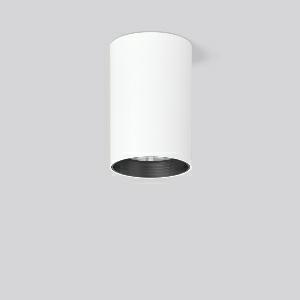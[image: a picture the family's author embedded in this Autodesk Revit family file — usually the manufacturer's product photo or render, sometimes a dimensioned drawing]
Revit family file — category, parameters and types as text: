
# Revit family: heledon_maxi_a_931229_002_2_c568
name_source: partatom
category: Lighting Fixtures
units: mm (PartAtom-declared; Revit-internal decimal feet)

## family parameters
Cut with Voids When Loaded = No
Host = Face
Light Source = No
Part Type = Normal
Room Calculation Point = No
Round Connector Dimension = Use Diameter
Shared = No

## types (1)
- HELEDON maxi A (1 x LED Modul 927, 3450 lm, 2700)
    Apparent Load = 35 VA
    Approval mark = CE
    CIE Flux Codes = 96 100 100 100 100
    Color Rendering = 92
    Color Temperature = 2700
    Default Elevation = 1800 mm
    Description = Series: HELEDON maxi
Cylindrical surface-mounted downlight. Housing: die-cast aluminium, powder-coated. Internal ceiling frame polycarbonate with bayonet mounting. Black plastic ring and recessed LED to prevent glare from the side. Optical assembly with lens made of plastic (polycarbonate) for the best homogeneous light distribution - can be changed without tools. Best colour rendering index Ra>90. Suitable for Ceiling mounting. Easy installation with a separate ceiling frame with bayonet mounting and plug connection. Driver integrated. Connected via plug-in connector. High quality converter without flickering and stroboscopic effect. The following accessories can be mounted without use of tools: interchangeable lenses, decorative glasses, honeycomb louvre, clear and frosted diffusers, white interchangeable plastic ring. 
Colour: traffic white, matt (RAL 9016)
Diameter: 123 mm
Height: 183 mm
Lamp: LED
Socket: without socket
Colour temperature: 2700K
Colour rendering index (CRI): 92
System power: 35 W
Rated luminous flux: 3450 lm
Luminous efficiency: 99 lm/W
Control gear: Regulated power supply
Protection class: I
Type of protection: IP 20
    Height = 183 mm
    Lamp = 1 x LED Modul 927
    Lamp Light Flux = 3450 lm
    Lamp count = 1
    Length = 123 mm
    Lifetime = 50000 h
    Luminous efficacy = 99 lm/W
    Manufacturer = RZB
    ModVariant = No
    Model = 931229.002.2
    Mounting Place = Ceiling
    Mounting Type = Surface mounted
    Number of Poles = 1
    OnlyDefault = Yes
    Power Factor = 1
    Product Name = HELEDON maxi A
    Product group = Surface mounted downlights
    ProductGroupID = 302
    Protection Class = Protection class I
    Protection Degree = IP 20
    RLX_Detail_Level = 1
    RLX_Emergency_Light_Flux = 0 lm
    RLX_Emergency_Type = 0
    RLX_Emergency_Type_DB = No
    RlxData = <blob elided: 96509 chars, md5=ee0cedda>
    Socket = socket
    Standby Power = 0 W
    System Light Flux = 3450 lm
    System Power = 35 W
    Type Comments = Product without accessories
    Type Image = 931193.002.jpg
    URL = http://relux.com
    VarID = ---
    Voltage = 230 V
    Voltage Range = 220-240 V
    Weight = 0.00 kg
    Width = 0 mm  [stored 0 ft]

note: [stored X ft] marks values corroborated as IEEE doubles in the binary element streams (Revit-internal decimal feet)

## geometry (parser evidence)
native form markers: Blend x4, Sweep x9
no freeform markers — native parametric forms only
